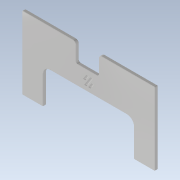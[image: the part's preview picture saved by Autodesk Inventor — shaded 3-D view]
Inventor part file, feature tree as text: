
AUTODESK INVENTOR PART (.ipt)
format: ipt  version: 2022.1 (Build 261234020, 234B)  size: 528,896 bytes
history: native  units: mm
features: reference x4, other x4, move_body x4, delete_face x3, direct_edit x3, chamfer x3, extrude x1, fillet x1, sketch x1
ambient origin geometry x8: Origin, YZ Plane, XZ Plane, XY Plane, X Axis, Y Axis, Z Axis, Center Point
bodies: Volumenkörper1 (feature_tree)
feature tree (24):
  delete_face  "Fläche löschen1"
  extrude  "Extrusion1"  TaperAngle=0.0deg  [1 undecoded]
  direct_edit  "Direktbearbeitung1"
  chamfer  "Fase1"  Distance=1.0mm Angle=45.0deg
  chamfer  "Fase2"  Distance=2.0mm Angle=45.0deg
  direct_edit  "Direktbearbeitung2"
  delete_face  "Fläche löschen2"
  delete_face  "Fläche löschen3"
  fillet  "Rundung1"  Radius=1.5mm
  chamfer  "Fase3"  Distance=2.0mm
  direct_edit  "Direktbearbeitung3"
  sketch  "Skizze1"  dims[d0=3.2mm d1=0.0mm d2=0.0mm d3=0.0mm d4=-1.0mm d5=1.0mm d6=2.0mm d7=45.0deg d8=0.2mm d9=2.0mm d10=45.0deg d11=0.0mm d12=0.0mm d13=1.5mm d14=2.0mm d15=0.4mm d16=2.0mm d17=45.0deg d18=0.0mm d19=0.0mm d20=-0.5mm d21=0.0mm d22=0.0mm d23=-0.5mm]
  reference  "Referenz1"
  reference  "Referenz2"
  reference  "Referenz3"
  reference  "Referenz4"
  other  "cover"
  other  "<userpath>\Desktop\RAMA_SBNG\BedPan\Ramabed.iam"
  other  "Ramabed.iam"
  other  "Ramabed wago mount:1"
  move_body  "Verschieben1"
  move_body  "Verschieben2"
  move_body  "Verschieben3"
  move_body  "Verschieben4"
note: 1 required parameter value undecoded (feature->parameter linkage not recoverable at this tier; creation-order binding heuristic only, values carry confidence <= 0.55)
